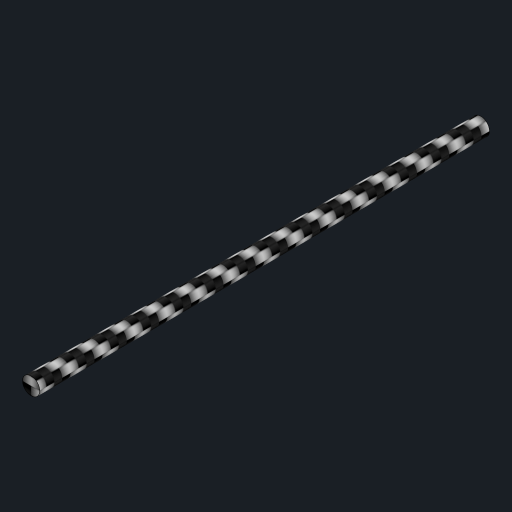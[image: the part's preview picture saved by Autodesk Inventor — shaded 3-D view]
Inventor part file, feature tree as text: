
AUTODESK INVENTOR PART (.ipt)
format: ipt  version: 2023 (Build 270158000, 158)  size: 110,080 bytes
history: native  units: in
note: dims shown in document units (in); Inventor stores cm internally (conversion verified against a paired STEP export)
features: other x1, extrude x1, sketch x1
ambient origin geometry x8: Origin, YZ Plane, XZ Plane, XY Plane, X Axis, Y Axis, Z Axis, Center Point
bodies: Body1 (feature_tree)
feature tree (3):
  other  "ソリッド1"
  extrude  "押し出し1"  Depth=0.0787in
  sketch  "スケッチ1"
